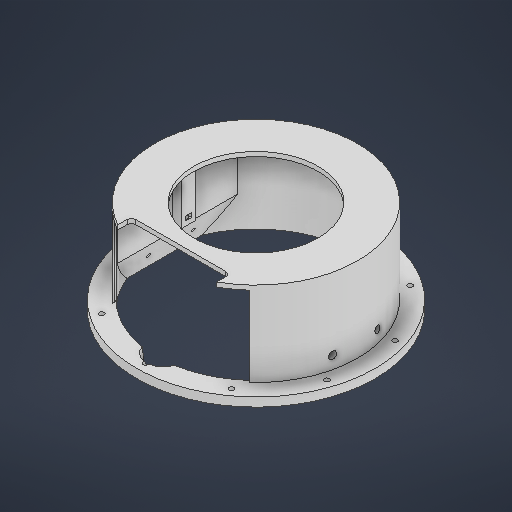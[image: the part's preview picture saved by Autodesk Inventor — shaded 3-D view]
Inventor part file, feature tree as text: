
AUTODESK INVENTOR PART (.ipt)
format: ipt  version: 2025 (Build 290162000, 162)  size: 450,048 bytes
history: native  units: in
note: dims shown in document units (in); Inventor stores cm internally (conversion verified against a paired STEP export)
features: extrude x15, sketch x13, plane x3, fillet x1, chamfer x1
ambient origin geometry x8: Origin, YZ Plane, XZ Plane, XY Plane, X Axis, Y Axis, Z Axis, Center Point
bodies: Solid1 (feature_tree)
feature tree (33):
  sketch  "Sketch1"  dims[d5=0.0in d7=0.0in]
  extrude  "Extrusion1"  TaperAngle=0.0deg  [1 undecoded]
  extrude  "Extrusion2"  Depth=4.5276in
  extrude  "Extrusion7"  Depth=0.2165in
  extrude  "Extrusion34"  Depth=6.1024in
  sketch  "Sketch30"  dims[d272=3.937in d273=4.1535in d274=0.0in d285=3.937in]
  plane  "Work Plane19"
  plane  "Work Plane21"
  plane  "Work Plane22"
  extrude  "Extrusion36"  Depth=4.1535in TaperAngle=0.0deg
  fillet  "Fillet19"  Radius=3.937in
  extrude  "Extrusion37"  Depth=2.0812in TaperAngle=0.0deg
  extrude  "Extrusion38"  Depth=0.1969in
  sketch  "Sketch35"  dims[d293=0.1969in d294=0.1969in]
  extrude  "Extrusion40"  Depth=1.5748in
  extrude  "Extrusion41"  Depth=0.1969in
  extrude  "Extrusion42"  Depth=0.3937in TaperAngle=0.0deg
  extrude  "Extrusion43"  Depth=1.7717in TaperAngle=0.0deg
  chamfer  "Chamfer14"  Distance=0.2805in
  sketch  "Sketch38"  dims[d301=2.9528in]
  extrude  "Extrusion44"  Depth=0.315in TaperAngle=0.0deg
  extrude  "Extrusion45"  Depth=0.315in
  sketch  "Sketch39"  dims[d308=6.378in d309=0.2805in d310=0.5906in d311=0.0in d312=6.8898in d313=5.5413in d314=0.2362in d315=0.1969in d316=0.0in d317=0.1969in d318=0.0in d319=1.378in d320=0.0in d321=0.5906in d322=1.378in d323=45.0deg d324=1.0in d326=0.315in d328=0.0in d329=0.0in d330=0.1772in d331=0.315in d332=0.0in d333=1.0in d334=0.2953in d335=0.1772in d336=0.0in d337=0.0in d338=0.315in d339=0.0in d113=0.0197in d114=0.0344in d115=0.0197in d116=0.0344in d167=0.0197in d168=0.0344in d169=0.0197in d170=0.0344in d215=0.0197in d216=0.0344in d217=0.0197in d218=0.0344in d219=0.0in d220=0.0in d254=0.0197in d255=0.0344in d256=0.0197in d257=0.0344in]
  extrude  "Extrusion46"  Depth=0.315in
  extrude  "Extrusion47"  Depth=0.315in TaperAngle=0.0deg
  sketch  "Sketch2"  dims[d18=0.0in d52=4.5276in]
  sketch  "Sketch Circular Pattern5"  dims[d264=9.8425in d265=0.2165in]
  sketch  "Sketch28"  dims[d266=3.937in d268=360.0deg d271=6.1024in]
  sketch  "Sketch31"  dims[d286=1.5748in d287=2.0812in d288=0.0in]
  sketch  "Sketch32"  dims[d289=3.5039in d290=0.1969in]
  sketch  "Sketch33"  dims[d291=4.4094in d292=1.5748in]
  sketch  "Sketch36"  dims[d295=3.3465in d296=0.3937in d297=0.0in]
  sketch  "Sketch37"  dims[d298=0.6299in d299=1.7717in d300=0.0in]
note: 1 required parameter value undecoded (feature->parameter linkage not recoverable at this tier; creation-order binding heuristic only, values carry confidence <= 0.55)
